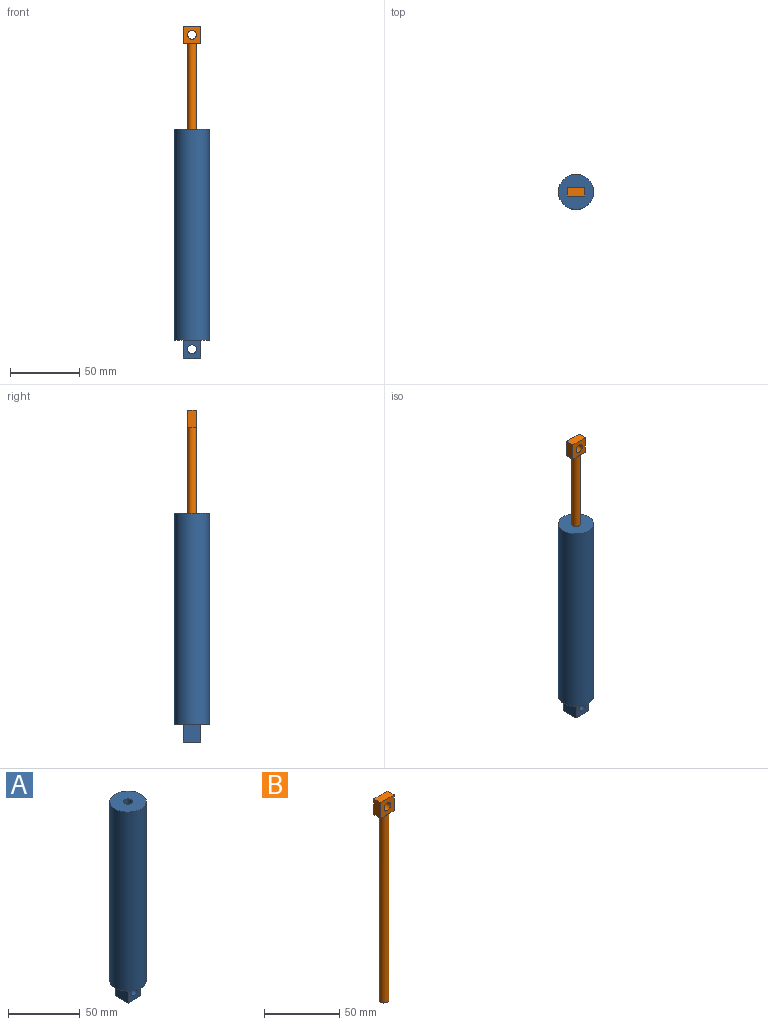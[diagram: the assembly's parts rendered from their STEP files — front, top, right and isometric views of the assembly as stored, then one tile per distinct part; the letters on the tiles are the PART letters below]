
ASSEMBLY  parts=2 mates=1
PART A: 11 faces, bbox 25.4x25.4x165.1 mm
  f0: cylinder r=3.17mm len=152.4mm, axis (0,0,-1), area 3040.2mm2, adj f2,f10
  f1: cylinder r=12.7mm len=152.4mm, axis (0,0,-1), area 12161mm2, adj f2,f3
  f2: plane 25.4x25.4mm, normal (0,0,1), area 475mm2, adj f0,f1
  f3: plane 25.4x25.4mm, normal (0,0,-1), area 345.4mm2, adj f1,f4,f5,f6,f9
  f4: plane 12.7x12.7mm, normal (0,-1,0), area 129.6mm2, adj f3,f6,f7,f8,f9
  f5: plane 12.7x12.7mm, normal (0,1,0), area 129.6mm2, adj f3,f6,f7,f8,f9
  f6: plane 12.7x12.7mm, normal (1,0,0), area 161.3mm2, adj f3,f4,f5,f8
  f7: cylinder r=3.17mm len=12.7mm, axis (0,-1,0), area 253.4mm2, adj f4,f5
  f8: plane 12.7x12.7mm, normal (0,0,-1), area 161.3mm2, adj f4,f5,f6,f9
  f9: plane 12.7x12.7mm, normal (-1,0,0), area 161.3mm2, adj f3,f4,f5,f8
  f10: plane 6.35x6.35mm, normal (0,0,1), area 31.7mm2, adj f0
PART B: 10 faces, bbox 12.7x6.4x165.1 mm
  f0: cylinder r=3.17mm len=152.4mm, axis (0,0,-1), area 3040.2mm2, adj f1,f2,f3
  f1: plane 6.35x6.35mm, normal (0,0,-1), area 31.7mm2, adj f0
  f2: plane 6.35x6.35mm, normal (0,0,-1), area 24.5mm2, adj f0,f4,f5,f6
  f3: plane 6.35x6.35mm, normal (0,0,-1), area 24.5mm2, adj f0,f4,f6,f7
  f4: plane 12.7x12.7mm, normal (0,1,0), area 129.6mm2, adj f2,f3,f5,f7,f8,f9
  f5: plane 12.7x6.35mm, normal (-1,0,0), area 80.6mm2, adj f2,f4,f6,f8
  f6: plane 12.7x12.7mm, normal (0,-1,0), area 129.6mm2, adj f2,f3,f5,f7,f8,f9
  f7: plane 12.7x6.35mm, normal (1,0,0), area 80.6mm2, adj f3,f4,f6,f8
  f8: plane 12.7x6.35mm, normal (0,0,1), area 80.6mm2, adj f4,f5,f6,f7
  f9: cylinder r=3.17mm len=6.35mm, axis (0,-1,0), area 126.7mm2, adj f4,f6
PLACE A t=(-70.05,-12.26,-5.09)mm
PLACE B t=(-124,-68.42,56.65)mm
MATE slider B.f0 <-> A.f1  axis (0,0,-1) through (-70.05,-12.26,132.85)mm
